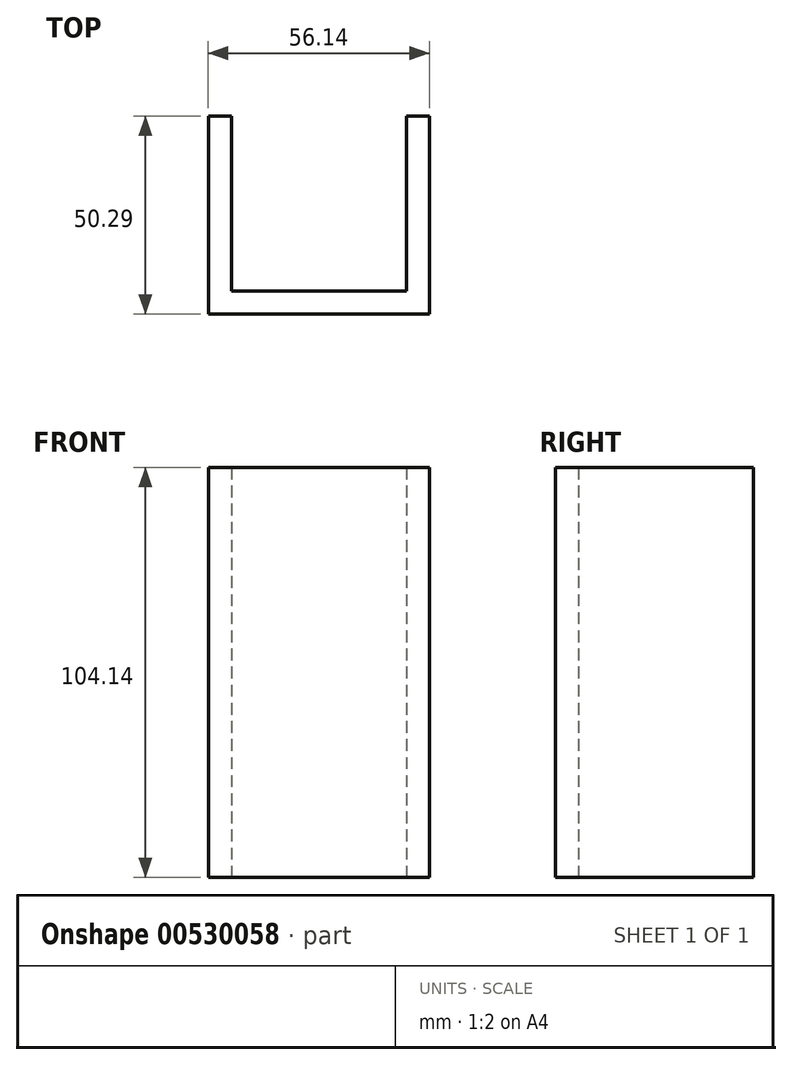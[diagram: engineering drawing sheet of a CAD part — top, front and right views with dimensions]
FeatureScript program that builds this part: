
annotation { "Feature Type Name" : "Feature", "Feature Type Description" : "" }
export const myFeature = defineFeature(function(context is Context, id is Id, definition is map)
    precondition{}
    {
        {
            var Q0;
            Q0=qCreatedBy(makeId("Top.planeOp"),FACE);
            var sketch = newSketch(context, id + "F0", { "sketchPlane" : qUnion([Q0])});
            skLineSegment(sketch, "E0", {"start": v(-14.61, -7.73) * mm, "end": v(29.84, -7.73) * mm});
            skLineSegment(sketch, "E1", {"start": v(29.84, -7.73) * mm, "end": v(29.84, 36.72) * mm});
            skLineSegment(sketch, "E2", {"start": v(29.84, 36.72) * mm, "end": v(35.68, 36.72) * mm});
            skLineSegment(sketch, "E3", {"start": v(35.68, 36.72) * mm, "end": v(35.68, -13.57) * mm});
            skLineSegment(sketch, "E4", {"start": v(35.68, -13.57) * mm, "end": v(-20.46, -13.57) * mm});
            skLineSegment(sketch, "E5", {"start": v(-14.61, -7.73) * mm, "end": v(-14.61, 36.72) * mm});
            skLineSegment(sketch, "E6", {"start": v(-14.61, 36.72) * mm, "end": v(-20.46, 36.72) * mm});
            skLineSegment(sketch, "E7", {"start": v(-20.46, 36.72) * mm, "end": v(-20.46, -13.57) * mm});
            skSolve(sketch);
        }
        {
            var Q0;
            Q0=qSketchRegion(id+"F0",true);
            extrude(context, id + "F1", {"entities" : qUnion([Q0]), "depth" : 104.14 * mm, "offsetDistance" : 25.4 * mm});
        }
    });
